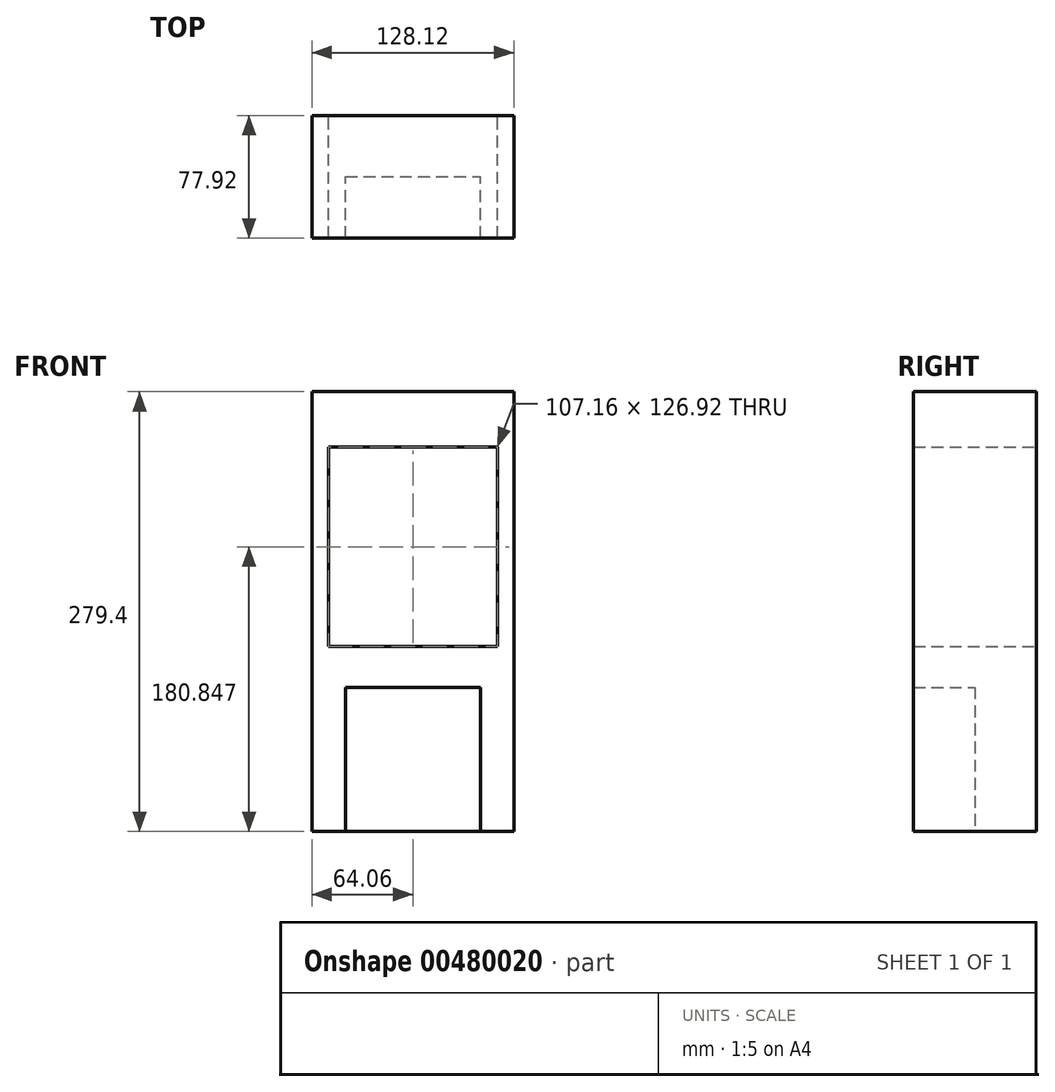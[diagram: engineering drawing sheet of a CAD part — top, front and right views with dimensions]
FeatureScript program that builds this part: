
annotation { "Feature Type Name" : "Feature", "Feature Type Description" : "" }
export const myFeature = defineFeature(function(context is Context, id is Id, definition is map)
    precondition{}
    {
        {
            var Q0;
            Q0=qCreatedBy(makeId("Top.planeOp"),FACE);
            var sketch = newSketch(context, id + "F0", { "sketchPlane" : qUnion([Q0])});
            skLineSegment(sketch, "E0.bottom", {"start": v(64.06, -38.96) * mm, "end": v(-64.06, -38.96) * mm});
            skLineSegment(sketch, "E0.top", {"start": v(64.06, 38.96) * mm, "end": v(-64.06, 38.96) * mm});
            skLineSegment(sketch, "E0.left", {"start": v(64.06, -38.96) * mm, "end": v(64.06, 38.96) * mm});
            skLineSegment(sketch, "E0.right", {"start": v(-64.06, -38.96) * mm, "end": v(-64.06, 38.96) * mm});
            skPoint(sketch, "E0.middle", {"position": v(0, 0) * mm});
            skSolve(sketch);
        }
        {
            var Q0;
            Q0=makeQuery(id+"F0.imprint","IMPRINT",FACE,{"disambiguationData":[TD([[makeQuery(id+"F0.imprint","IMPRINT",EDGE,{"derivedFrom":sQuery(id+"F0.wireOp",EDGE,"E0.bottom")}),-1.0]])]});
            extrude(context, id + "F1", {"entities" : qUnion([Q0]), "depth" : 254 * mm, "hasSecondDirection" : true, "secondDirectionOppositeDirection" : true, "secondDirectionDepth" : 25.4 * mm});
        }
        {
            var Q0;
            Q0=qCreatedBy(makeId("Front.planeOp"),FACE);
            var sketch = newSketch(context, id + "F2", { "sketchPlane" : qUnion([Q0])});
            skLineSegment(sketch, "E1.bottom", {"start": v(42.78, 66.16) * mm, "end": v(-42.78, 66.16) * mm});
            skLineSegment(sketch, "E1.top", {"start": v(42.78, -66.16) * mm, "end": v(-42.78, -66.16) * mm});
            skLineSegment(sketch, "E1.left", {"start": v(42.78, 66.16) * mm, "end": v(42.78, -66.16) * mm});
            skLineSegment(sketch, "E1.right", {"start": v(-42.78, 66.16) * mm, "end": v(-42.78, -66.16) * mm});
            skPoint(sketch, "E1.middle", {"position": v(0, 0) * mm});
            skSolve(sketch);
        }
        {
            var Q0;
            Q0 = qSketchRegion(id + "F2", true);
            var Q1;
            Q1=sQuery(id+"F2.wireOp",EDGE,"E1.top");
            extrude(context, id + "F3", {"entities" : qUnion([Q0]), "operationType" : NewBodyOperationType.REMOVE, "surfaceEntities" : qUnion([Q1]), "depth" : 254 * mm});
        }
        {
            var Q0;
            Q0=qCreatedBy(makeId("Front.planeOp"),FACE);
            var sketch = newSketch(context, id + "F4", { "sketchPlane" : qUnion([Q0])});
            skLineSegment(sketch, "E2.bottom", {"start": v(-53.58, 91.99) * mm, "end": v(53.58, 91.99) * mm});
            skLineSegment(sketch, "E2.top", {"start": v(-53.58, 218.9) * mm, "end": v(53.58, 218.9) * mm});
            skLineSegment(sketch, "E2.left", {"start": v(-53.58, 91.99) * mm, "end": v(-53.58, 218.9) * mm});
            skLineSegment(sketch, "E2.right", {"start": v(53.58, 91.99) * mm, "end": v(53.58, 218.9) * mm});
            skPoint(sketch, "E2.middle", {"position": v(0, 155.45) * mm});
            skSolve(sketch);
        }
        {
            var Q0;
            Q0 = qSketchRegion(id + "F4", true);
            extrude(context, id + "F5", {"entities" : qUnion([Q0]), "operationType" : NewBodyOperationType.REMOVE, "endBound" : BoundingType.SYMMETRIC, "depth" : 254 * mm});
        }
    });
